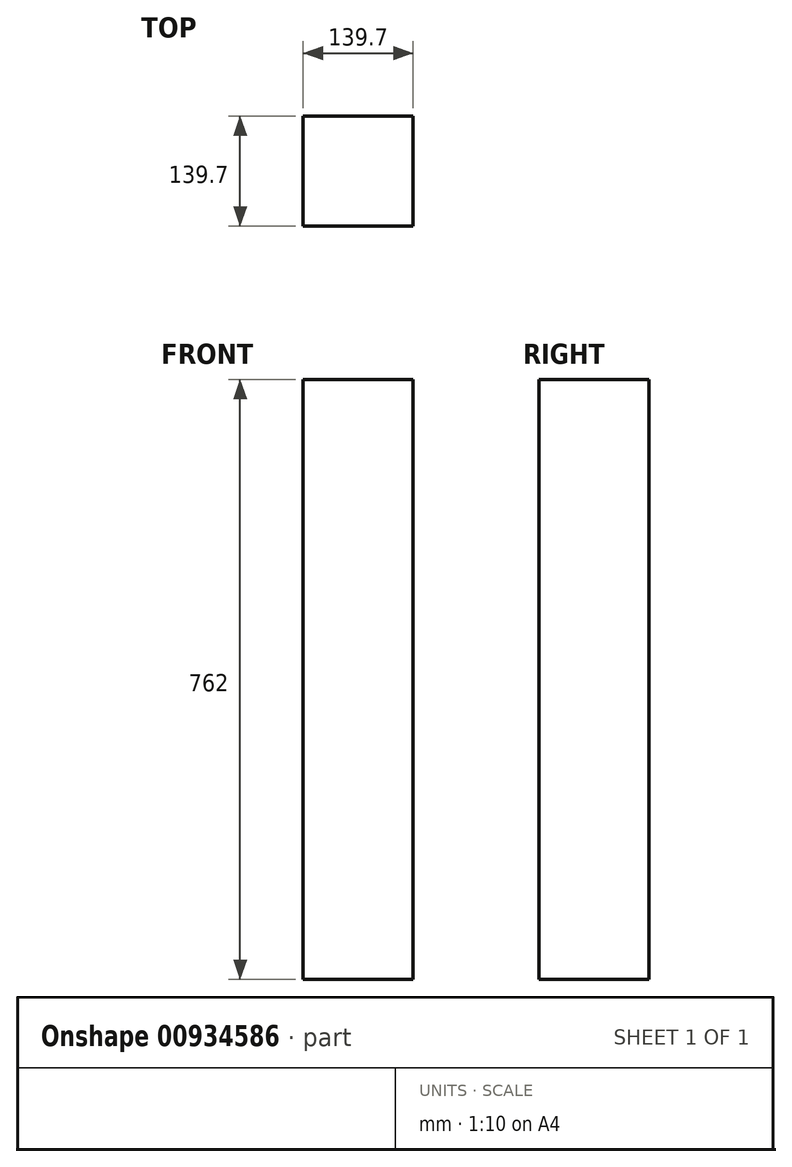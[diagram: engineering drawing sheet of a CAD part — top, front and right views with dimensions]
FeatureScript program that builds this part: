
annotation { "Feature Type Name" : "Feature", "Feature Type Description" : "" }
export const myFeature = defineFeature(function(context is Context, id is Id, definition is map)
    precondition{}
    {
        {
            var Q0;
            Q0=qCreatedBy(makeId("Top.planeOp"),FACE);
            var sketch = newSketch(context, id + "F0", { "sketchPlane" : qUnion([Q0])});
            skLineSegment(sketch, "E0.bottom", {"start": v(2477.3, -1432.22) * mm, "end": v(2617, -1432.22) * mm});
            skLineSegment(sketch, "E0.top", {"start": v(2477.3, -1571.92) * mm, "end": v(2617, -1571.92) * mm});
            skLineSegment(sketch, "E0.left", {"start": v(2477.3, -1432.22) * mm, "end": v(2477.3, -1571.92) * mm});
            skLineSegment(sketch, "E0.right", {"start": v(2617, -1432.22) * mm, "end": v(2617, -1571.92) * mm});
            skSolve(sketch);
        }
        {
            var Q0;
            Q0=makeQuery(id+"F0.imprint","IMPRINT",FACE,{"disambiguationData":[TD([[makeQuery(id+"F0.imprint","IMPRINT",EDGE,{"derivedFrom":sQuery(id+"F0.wireOp",EDGE,"E0.bottom")}),-1.0]])]});
            extrude(context, id + "F1", {"entities" : qUnion([Q0]), "depth" : 762 * mm, "offsetDistance" : 25.4 * mm});
        }
    });
